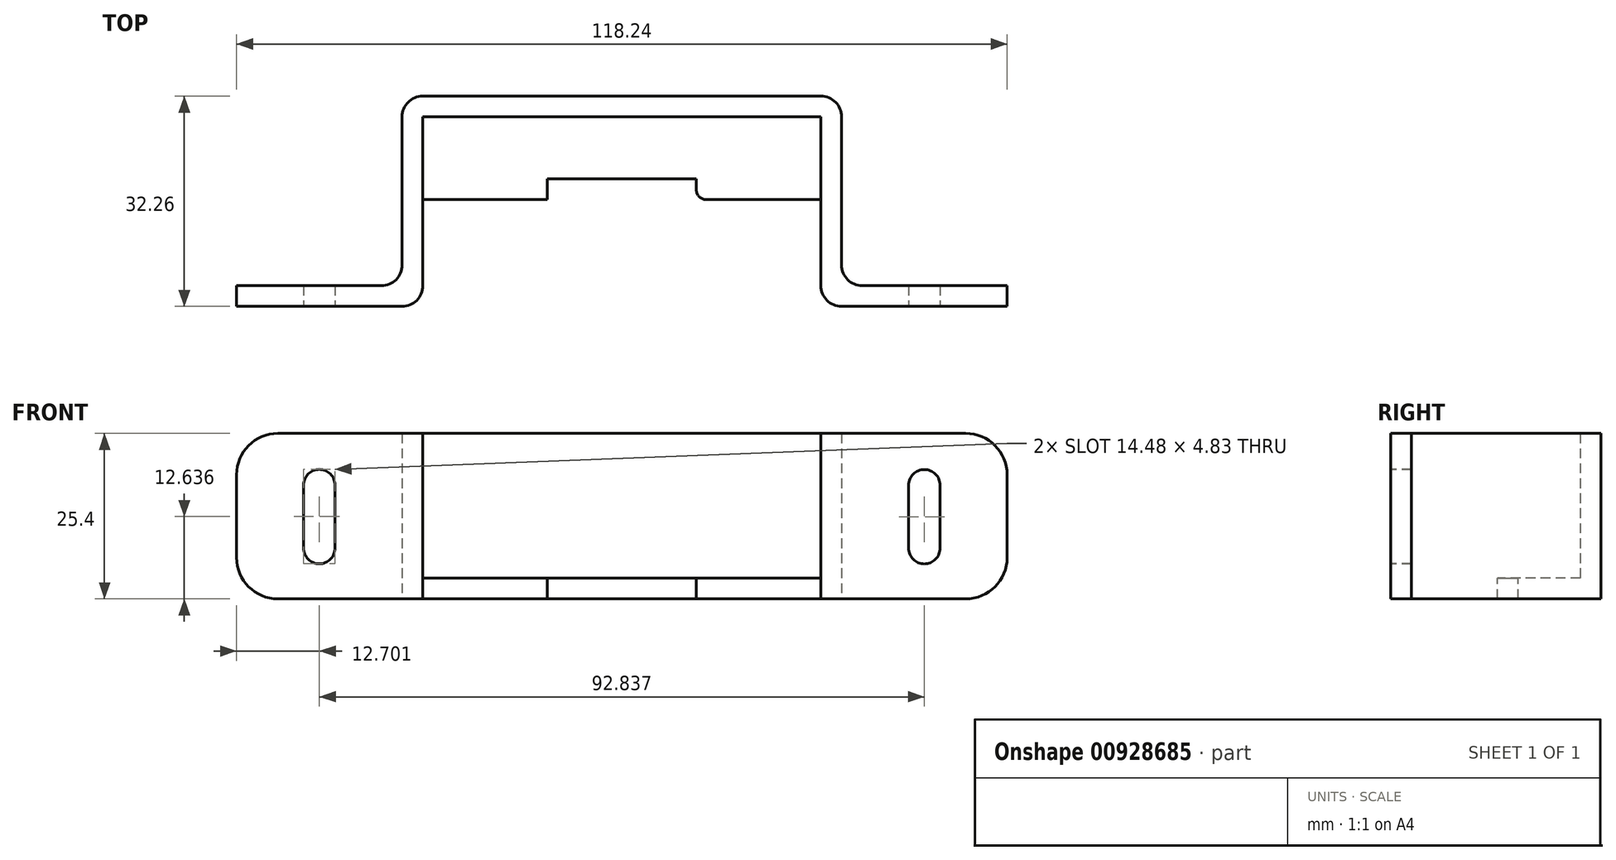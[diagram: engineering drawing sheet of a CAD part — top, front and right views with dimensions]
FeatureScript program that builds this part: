
annotation { "Feature Type Name" : "Feature", "Feature Type Description" : "" }
export const myFeature = defineFeature(function(context is Context, id is Id, definition is map)
    precondition{}
    {
        {
            var Q0;
            Q0=qCreatedBy(makeId("Top.planeOp"),FACE);
            var sketch = newSketch(context, id + "F0", { "sketchPlane" : qUnion([Q0])});
            skLineSegment(sketch, "E0", {"start": v(0, 29.08) * mm, "end": v(30.54, 29.08) * mm});
            skLineSegment(sketch, "E1", {"start": v(30.54, 29.08) * mm, "end": v(30.54, 0) * mm});
            skLineSegment(sketch, "E2", {"start": v(30.54, 0) * mm, "end": v(59.12, 0) * mm});
            skLineSegment(sketch, "E3.0", {"start": v(33.72, 3.17) * mm, "end": v(59.12, 3.17) * mm});
            skLineSegment(sketch, "E3.1", {"start": v(33.72, 32.26) * mm, "end": v(33.72, 3.18) * mm});
            skLineSegment(sketch, "E3.2", {"start": v(0, 32.26) * mm, "end": v(33.72, 32.26) * mm});
            skLineSegment(sketch, "E4", {"start": v(59.12, 3.18) * mm, "end": v(59.12, 0) * mm});
            skLineSegment(sketch, "E5.MirrorCS", {"start": v(-59.12, 3.18) * mm, "end": v(-59.12, 0) * mm});
            skLineSegment(sketch, "E6.MirrorCS", {"start": v(-30.54, 29.08) * mm, "end": v(-30.54, 0) * mm});
            skLineSegment(sketch, "E7.MirrorCS", {"start": v(0, 32.26) * mm, "end": v(-33.72, 32.26) * mm});
            skLineSegment(sketch, "E8.MirrorCS", {"start": v(-33.72, 3.17) * mm, "end": v(-59.12, 3.17) * mm});
            skLineSegment(sketch, "E9.MirrorCS", {"start": v(-30.54, 0) * mm, "end": v(-59.12, 0) * mm});
            skLineSegment(sketch, "E10.MirrorCS", {"start": v(0, 29.08) * mm, "end": v(-30.54, 29.08) * mm});
            skLineSegment(sketch, "E11.MirrorCS", {"start": v(-33.72, 32.26) * mm, "end": v(-33.72, 3.18) * mm});
            skSolve(sketch);
        }
        {
            var Q0;
            Q0=qSketchRegion(id+"F0",true);
            extrude(context, id + "F1", {"entities" : qUnion([Q0]), "depth" : 25.4 * mm, "offsetDistance" : 25.4 * mm});
        }
        {
            var Q0;
            Q0=makeQuery(id+"F1.opExtrude","SWEPT_EDGE",EDGE,{"disambiguationData":[OSD([sQuery(id+"F0.wireOp",EDGE,"E6.MirrorCS"),sQuery(id+"F0.wireOp",EDGE,"E9.MirrorCS")])]});
            var Q1;
            Q1=makeQuery(id+"F1.opExtrude","SWEPT_EDGE",EDGE,{"disambiguationData":[OSD([sQuery(id+"F0.wireOp",EDGE,"E1"),sQuery(id+"F0.wireOp",EDGE,"E2")])]});
            fillet(context, id + "F2", {"entities" : qUnion([Q0, Q1]), "radius" : 3.17 * mm, "tangentPropagation" : true, "allowEdgeOverflow" : false});
        }
        {
            var Q0;
            Q0=qCreatedBy(makeId("Front.planeOp"),FACE);
            var sketch = newSketch(context, id + "F3", { "sketchPlane" : qUnion([Q0])});
            skLineSegment(sketch, "E12", {"start": v(-46.42, 7.81) * mm, "end": v(-46.42, 17.46) * mm});
            skArc(sketch, "E13.0.startCap", {"start": v(-44, 7.81) * mm, "mid": v(-46.42, 5.4) * mm, "end": v(-48.83, 7.81) * mm});
            skArc(sketch, "E13.0.endCap", {"start": v(-48.83, 17.46) * mm, "mid": v(-46.42, 19.88) * mm, "end": v(-44, 17.46) * mm});
            skLineSegment(sketch, "E13.0.left", {"start": v(-48.83, 7.81) * mm, "end": v(-48.83, 17.46) * mm});
            skLineSegment(sketch, "E13.0.right", {"start": v(-44, 7.81) * mm, "end": v(-44, 17.46) * mm});
            skLineSegment(sketch, "E14", {"start": v(46.42, 17.45) * mm, "end": v(46.42, 7.8) * mm});
            skArc(sketch, "E15.0.startCap", {"start": v(44, 17.45) * mm, "mid": v(46.42, 19.86) * mm, "end": v(48.83, 17.45) * mm});
            skArc(sketch, "E15.0.endCap", {"start": v(48.83, 7.8) * mm, "mid": v(46.42, 5.38) * mm, "end": v(44, 7.8) * mm});
            skLineSegment(sketch, "E15.0.left", {"start": v(48.83, 17.45) * mm, "end": v(48.83, 7.8) * mm});
            skLineSegment(sketch, "E15.0.right", {"start": v(44, 17.45) * mm, "end": v(44, 7.8) * mm});
            skSolve(sketch);
        }
        {
            var Q0;
            Q0=qSketchRegion(id+"F3",true);
            extrude(context, id + "F4", {"entities" : qUnion([Q0]), "operationType" : NewBodyOperationType.REMOVE, "endBound" : BoundingType.THROUGH_ALL, "oppositeDirection" : true, "depth" : 25.4 * mm, "offsetDistance" : 25.4 * mm});
        }
        {
            var Q0;
            Q0=makeQuery(id+"F1.opExtrude","CAP_EDGE",EDGE,{"disambiguationData":[OSD([sQuery(id+"F0.wireOp",EDGE,"E5.MirrorCS")])],"isStart":true});
            var Q1;
            Q1=makeQuery(id+"F1.opExtrude","CAP_EDGE",EDGE,{"disambiguationData":[OSD([sQuery(id+"F0.wireOp",EDGE,"E5.MirrorCS")])],"isStart":false});
            var Q2;
            Q2=makeQuery(id+"F1.opExtrude","CAP_EDGE",EDGE,{"disambiguationData":[OSD([sQuery(id+"F0.wireOp",EDGE,"E4")])],"isStart":false});
            var Q3;
            Q3=makeQuery(id+"F1.opExtrude","CAP_EDGE",EDGE,{"disambiguationData":[OSD([sQuery(id+"F0.wireOp",EDGE,"E4")])],"isStart":true});
            fillet(context, id + "F5", {"entities" : qUnion([Q0, Q1, Q2, Q3]), "radius" : 6.35 * mm, "tangentPropagation" : true, "allowEdgeOverflow" : false});
        }
        {
            var Q0;
            Q0=makeQuery(id+"F1.opExtrude","CAP_FACE",FACE,{"disambiguationData":[OSD([sQuery(id+"F0.wireOp",EDGE,"E0"),sQuery(id+"F0.wireOp",EDGE,"E1"),sQuery(id+"F0.wireOp",EDGE,"E2"),sQuery(id+"F0.wireOp",EDGE,"E3.0"),sQuery(id+"F0.wireOp",EDGE,"E3.1"),sQuery(id+"F0.wireOp",EDGE,"E3.2"),sQuery(id+"F0.wireOp",EDGE,"E4"),sQuery(id+"F0.wireOp",EDGE,"E5.MirrorCS"),sQuery(id+"F0.wireOp",EDGE,"E6.MirrorCS"),sQuery(id+"F0.wireOp",EDGE,"E7.MirrorCS"),sQuery(id+"F0.wireOp",EDGE,"E8.MirrorCS"),sQuery(id+"F0.wireOp",EDGE,"E9.MirrorCS"),sQuery(id+"F0.wireOp",EDGE,"E10.MirrorCS"),sQuery(id+"F0.wireOp",EDGE,"E11.MirrorCS")])],"isStart":true});
            var sketch = newSketch(context, id + "F6", { "sketchPlane" : qUnion([Q0])});
            skLineSegment(sketch, "E16.bottom", {"start": v(-30.54, -29.08) * mm, "end": v(30.54, -29.08) * mm});
            skLineSegment(sketch, "E16.top", {"start": v(-30.54, -16.38) * mm, "end": v(30.54, -16.38) * mm});
            skLineSegment(sketch, "E16.left", {"start": v(-30.54, -29.08) * mm, "end": v(-30.54, -16.38) * mm});
            skLineSegment(sketch, "E16.right", {"start": v(30.54, -29.08) * mm, "end": v(30.54, -16.38) * mm});
            skSolve(sketch);
        }
        {
            var Q0;
            Q0=qSketchRegion(id+"F6",true);
            extrude(context, id + "F7", {"entities" : qUnion([Q0]), "operationType" : NewBodyOperationType.ADD, "oppositeDirection" : true, "depth" : 3.17 * mm, "offsetDistance" : 25.4 * mm});
        }
        {
            var Q0;
            Q0=makeQuery(id+"F1.opExtrude","SWEPT_EDGE",EDGE,{"disambiguationData":[OSD([sQuery(id+"F0.wireOp",EDGE,"E3.0"),sQuery(id+"F0.wireOp",EDGE,"E3.1")])]});
            var Q1;
            Q1=makeQuery(id+"F1.opExtrude","SWEPT_EDGE",EDGE,{"disambiguationData":[OSD([sQuery(id+"F0.wireOp",EDGE,"E3.1"),sQuery(id+"F0.wireOp",EDGE,"E3.2")])]});
            var Q2;
            Q2=makeQuery(id+"F1.opExtrude","SWEPT_EDGE",EDGE,{"disambiguationData":[OSD([sQuery(id+"F0.wireOp",EDGE,"E7.MirrorCS"),sQuery(id+"F0.wireOp",EDGE,"E11.MirrorCS")])]});
            var Q3;
            Q3=makeQuery(id+"F1.opExtrude","SWEPT_EDGE",EDGE,{"disambiguationData":[OSD([sQuery(id+"F0.wireOp",EDGE,"E8.MirrorCS"),sQuery(id+"F0.wireOp",EDGE,"E11.MirrorCS")])]});
            var Q4;
            Q4=makeQuery(id+"F7.opExtrude","SWEPT_EDGE",EDGE,{"disambiguationData":[OSD([sQuery(id+"F0.wireOp",EDGE,"E1"),sQuery(id+"F6.wireOp",EDGE,"E16.top"),sQuery(id+"F6.wireOp",EDGE,"E16.right")])]});
            var Q5;
            Q5=makeQuery(id+"F7.opExtrude","SWEPT_EDGE",EDGE,{"disambiguationData":[OSD([sQuery(id+"F0.wireOp",EDGE,"E6.MirrorCS"),sQuery(id+"F6.wireOp",EDGE,"E16.top"),sQuery(id+"F6.wireOp",EDGE,"E16.left")])]});
            fillet(context, id + "F8", {"entities" : qUnion([Q0, Q1, Q2, Q3, Q4, Q5]), "radius" : 3.17 * mm, "tangentPropagation" : true, "allowEdgeOverflow" : false});
        }
        {
            var Q0;
            Q0=makeQuery(id+"F7.opExtrude","CAP_FACE",FACE,{"disambiguationData":[OSD([sQuery(id+"F6.wireOp",EDGE,"E16.bottom"),sQuery(id+"F6.wireOp",EDGE,"E16.top"),sQuery(id+"F6.wireOp",EDGE,"E16.left"),sQuery(id+"F6.wireOp",EDGE,"E16.right")])],"isStart":false});
            var sketch = newSketch(context, id + "F9", { "sketchPlane" : qUnion([Q0])});
            skLineSegment(sketch, "E17.bottom", {"start": v(-11.43, 16.38) * mm, "end": v(11.43, 16.38) * mm});
            skLineSegment(sketch, "E17.top", {"start": v(-11.43, 19.56) * mm, "end": v(11.43, 19.56) * mm});
            skLineSegment(sketch, "E17.left", {"start": v(-11.43, 16.38) * mm, "end": v(-11.43, 19.56) * mm});
            skLineSegment(sketch, "E17.right", {"start": v(11.43, 16.38) * mm, "end": v(11.43, 19.56) * mm});
            skSolve(sketch);
        }
        {
            var Q0;
            Q0=qSketchRegion(id+"F9",true);
            extrude(context, id + "F10", {"entities" : qUnion([Q0]), "operationType" : NewBodyOperationType.REMOVE, "oppositeDirection" : true, "depth" : 25.4 * mm, "offsetDistance" : 25.4 * mm});
        }
        {
            var Q0;
            Q0=makeQuery(id+"F10.boolean.opBoolean","COPY",EDGE,{"derivedFrom":makeQuery(id+"F10.opExtrude","SWEPT_EDGE",EDGE,{"disambiguationData":[OSD([sQuery(id+"F6.wireOp",EDGE,"E16.top"),sQuery(id+"F9.wireOp",EDGE,"E17.bottom"),sQuery(id+"F9.wireOp",EDGE,"E17.left")])]})});
            var Q1;
            Q1=makeQuery(id+"F10.boolean.opBoolean","COPY",EDGE,{"derivedFrom":makeQuery(id+"F10.opExtrude","SWEPT_EDGE",EDGE,{"disambiguationData":[OSD([sQuery(id+"F6.wireOp",EDGE,"E16.top"),sQuery(id+"F9.wireOp",EDGE,"E17.bottom"),sQuery(id+"F9.wireOp",EDGE,"E17.right")])]})});
            fillet(context, id + "F11", {"entities" : qUnion([Q0, Q1]), "radius" : 1.52 * mm, "tangentPropagation" : true, "allowEdgeOverflow" : false});
        }
    });
